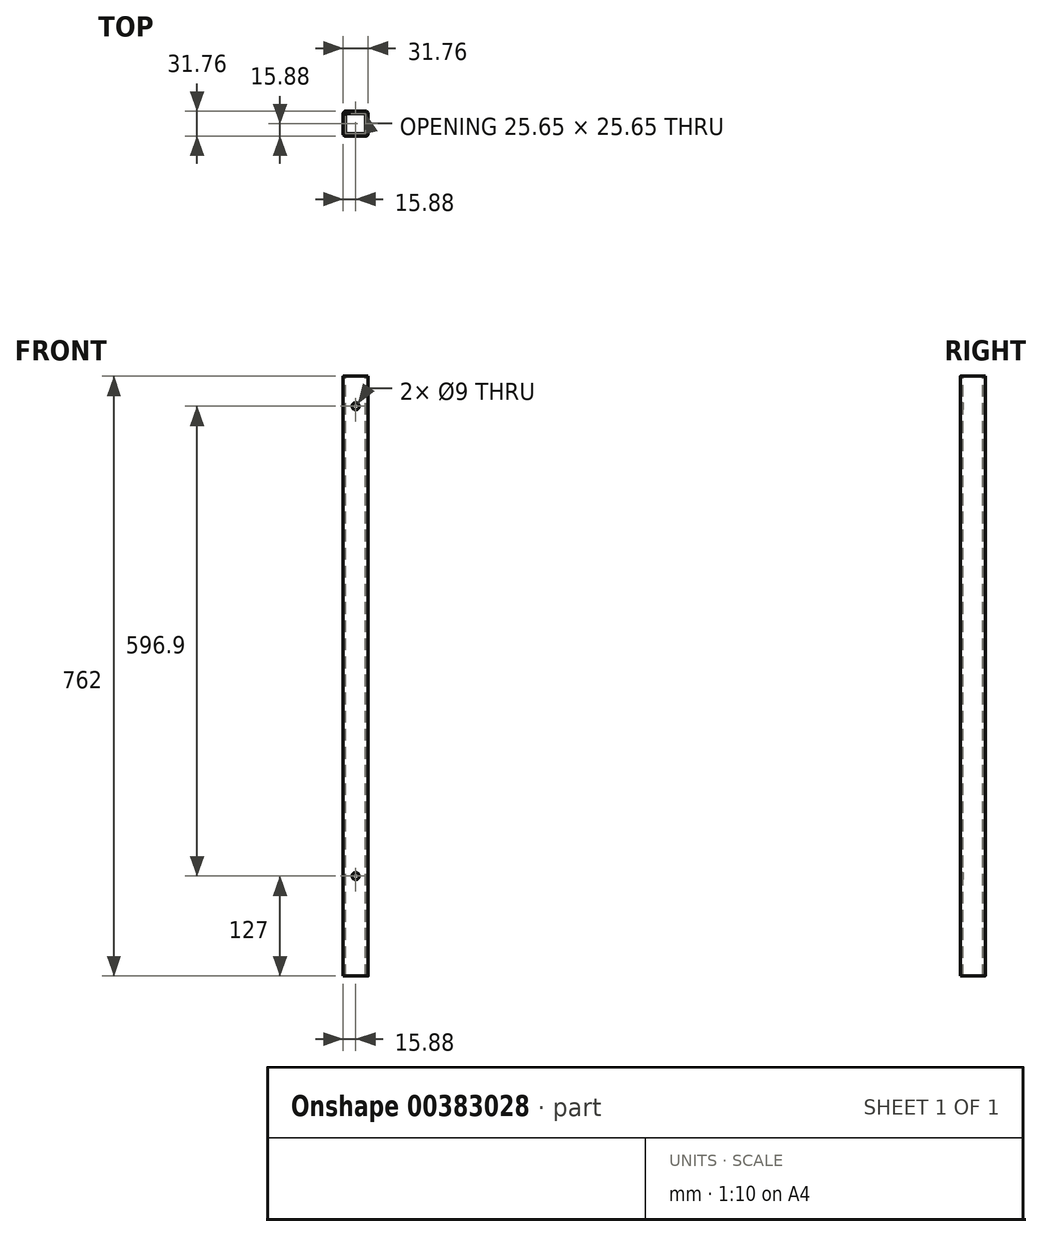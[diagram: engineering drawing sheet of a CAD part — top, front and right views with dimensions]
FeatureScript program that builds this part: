
annotation { "Feature Type Name" : "Feature", "Feature Type Description" : "" }
export const myFeature = defineFeature(function(context is Context, id is Id, definition is map)
    precondition{}
    {
        {
            var Q0;
            Q0=qCreatedBy(makeId("Top.planeOp"),FACE);
            var sketch = newSketch(context, id + "F0", { "sketchPlane" : qUnion([Q0])});
            skLineSegment(sketch, "E0.bottom", {"start": v(15.88, 15.88) * mm, "end": v(-15.88, 15.88) * mm});
            skLineSegment(sketch, "E0.top", {"start": v(15.88, -15.88) * mm, "end": v(-15.88, -15.88) * mm});
            skLineSegment(sketch, "E0.left", {"start": v(15.88, 15.88) * mm, "end": v(15.88, -15.88) * mm});
            skLineSegment(sketch, "E0.right", {"start": v(-15.88, 15.88) * mm, "end": v(-15.88, -15.88) * mm});
            skPoint(sketch, "E0.middle", {"position": v(0, 0) * mm});
            skSolve(sketch);
        }
        {
            var Q0;
            Q0=qSketchRegion(id+"F0",true);
            extrude(context, id + "F1", {"entities" : qUnion([Q0]), "oppositeDirection" : true, "depth" : 762 * mm});
        }
        {
            var Q0;
            Q0=makeQuery(id+"F1.opExtrude","SWEPT_EDGE",EDGE,{"disambiguationData":[OSD([sQuery(id+"F0.wireOp",EDGE,"E0.bottom"),sQuery(id+"F0.wireOp",EDGE,"E0.right")])]});
            var Q1;
            Q1=makeQuery(id+"F1.opExtrude","SWEPT_EDGE",EDGE,{"disambiguationData":[OSD([sQuery(id+"F0.wireOp",EDGE,"E0.top"),sQuery(id+"F0.wireOp",EDGE,"E0.right")])]});
            var Q2;
            Q2=makeQuery(id+"F1.opExtrude","SWEPT_EDGE",EDGE,{"disambiguationData":[OSD([sQuery(id+"F0.wireOp",EDGE,"E0.bottom"),sQuery(id+"F0.wireOp",EDGE,"E0.left")])]});
            var Q3;
            Q3=makeQuery(id+"F1.opExtrude","SWEPT_EDGE",EDGE,{"disambiguationData":[OSD([sQuery(id+"F0.wireOp",EDGE,"E0.top"),sQuery(id+"F0.wireOp",EDGE,"E0.left")])]});
            fillet(context, id + "F2", {"entities" : qUnion([Q0, Q1, Q2, Q3]), "radius" : 3.17 * mm, "tangentPropagation" : true, "allowEdgeOverflow" : false});
        }
        {
            var Q0;
            Q0=makeQuery(id+"F1.opExtrude","CAP_FACE",FACE,{"disambiguationData":[OSD([sQuery(id+"F0.wireOp",EDGE,"E0.bottom"),sQuery(id+"F0.wireOp",EDGE,"E0.top"),sQuery(id+"F0.wireOp",EDGE,"E0.left"),sQuery(id+"F0.wireOp",EDGE,"E0.right")])],"isStart":true});
            var Q1;
            Q1=makeQuery(id+"F1.opExtrude","CAP_FACE",FACE,{"disambiguationData":[OSD([sQuery(id+"F0.wireOp",EDGE,"E0.bottom"),sQuery(id+"F0.wireOp",EDGE,"E0.top"),sQuery(id+"F0.wireOp",EDGE,"E0.left"),sQuery(id+"F0.wireOp",EDGE,"E0.right")])],"isStart":false});
            shell(context, id + "F3", {"entities" : qUnion([Q0, Q1]), "thickness" : 3.05 * mm});
        }
        {
            var Q0;
            Q0=qCreatedBy(makeId("Front.planeOp"),FACE);
            var sketch = newSketch(context, id + "F4", { "sketchPlane" : qUnion([Q0])});
            skCircle(sketch, "E1", {"center": v(0, -38.1) * mm, "radius": 4.5 * mm});
            skCircle(sketch, "E2", {"center": v(0, -635) * mm, "radius": 4.5 * mm});
            skSolve(sketch);
        }
        {
            var Q0;
            Q0 = qSketchRegion(id + "F4", true);
            var Q1;
            Q1=makeQuery(id+"F1.opExtrude","SWEPT_FACE",FACE,{"disambiguationData":[OSD([sQuery(id+"F0.wireOp",EDGE,"E0.top")])]});
            extrude(context, id + "F5", {"entities" : qUnion([Q0]), "operationType" : NewBodyOperationType.REMOVE, "endBound" : BoundingType.UP_TO_SURFACE, "endBoundEntityFace" : qUnion([Q1]), "depth" : 25.4 * mm});
        }
    });
